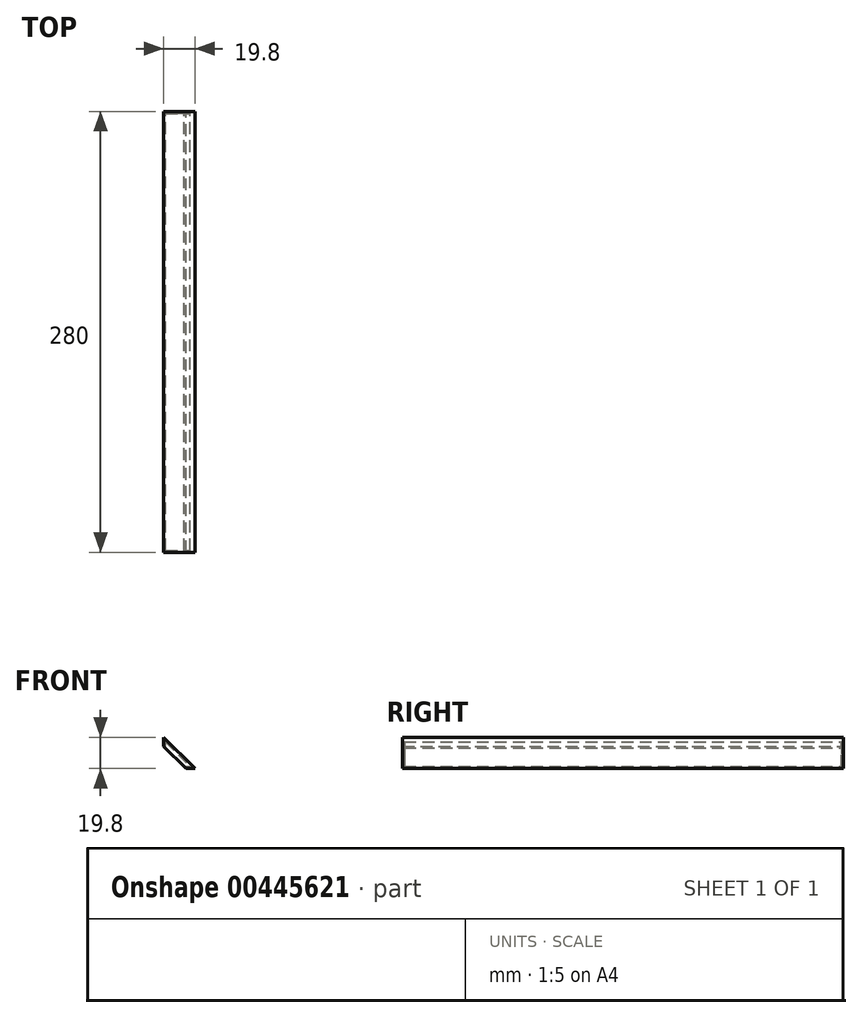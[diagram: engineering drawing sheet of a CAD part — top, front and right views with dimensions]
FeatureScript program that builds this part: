
annotation { "Feature Type Name" : "Feature", "Feature Type Description" : "" }
export const myFeature = defineFeature(function(context is Context, id is Id, definition is map)
    precondition{}
    {
        {
            var Q0;
            Q0=qCreatedBy(makeId("Front.planeOp"),FACE);
            var sketch = newSketch(context, id + "F0", { "sketchPlane" : qUnion([Q0])});
            skLineSegment(sketch, "E0.bottom", {"start": v(-9.9, -9.9) * mm, "end": v(9.9, -9.9) * mm});
            skLineSegment(sketch, "E0.top", {"start": v(-9.9, 9.9) * mm, "end": v(9.9, 9.9) * mm});
            skLineSegment(sketch, "E0.left", {"start": v(-9.9, -9.9) * mm, "end": v(-9.9, 9.9) * mm});
            skLineSegment(sketch, "E0.right", {"start": v(9.9, -9.9) * mm, "end": v(9.9, 9.9) * mm});
            skPoint(sketch, "E0.middle", {"position": v(0, 0) * mm});
            skLineSegment(sketch, "E1", {"start": v(-9.9, 9.9) * mm, "end": v(9.9, -9.9) * mm});
            skSolve(sketch);
        }
        {
            var Q0;
            Q0=makeQuery(id+"F0.imprint","IMPRINT",FACE,{"disambiguationData":[TD([[makeQuery(id+"F0.imprint","IMPRINT",EDGE,{"derivedFrom":sQuery(id+"F0.wireOp",EDGE,"E0.bottom")}),1.0]])]});
            extrude(context, id + "F1", {"entities" : qUnion([Q0]), "depth" : 280 * mm});
        }
        {
            var Q0;
            Q0=makeQuery(id+"F1.opExtrude","CAP_FACE",FACE,{"disambiguationData":[OSD([sQuery(id+"F0.wireOp",EDGE,"E0.bottom"),sQuery(id+"F0.wireOp",EDGE,"E0.left"),sQuery(id+"F0.wireOp",EDGE,"E1")])],"isStart":true});
            var sketch = newSketch(context, id + "F2", { "sketchPlane" : qUnion([Q0])});
            skLineSegment(sketch, "E2", {"start": v(-4.24, -9.9) * mm, "end": v(9.9, 4.24) * mm});
            skLineSegment(sketch, "E3.0.0", {"start": v(9.9, 9.9) * mm, "end": v(-9.9, -9.9) * mm});
            skLineSegment(sketch, "E3.0.1", {"start": v(-9.9, -9.9) * mm, "end": v(9.9, -9.9) * mm});
            skLineSegment(sketch, "E3.0.2", {"start": v(9.9, -9.9) * mm, "end": v(9.9, 9.9) * mm});
            skSolve(sketch);
        }
        {
            var Q0;
            {var subQ0=sQuery(id+"F2.wireOp",EDGE,"E2");Q0=makeQuery(id+"F2.imprint","IMPRINT",FACE,{"disambiguationData":[TD([[makeQuery(id+"F2.imprint","IMPRINT",EDGE,{"derivedFrom":subQ0}),-1.0]])]});}
            extrude(context, id + "F3", {"entities" : qUnion([Q0]), "operationType" : NewBodyOperationType.REMOVE, "oppositeDirection" : true, "depth" : 287 * mm});
        }
        {
            var Q0;
            Q0=makeQuery(id+"F3.boolean.opBoolean","COPY",FACE,{"derivedFrom":makeQuery(id+"F3.opExtrude","SWEPT_FACE",FACE,{"disambiguationData":[OSD([sQuery(id+"F2.wireOp",EDGE,"E2")])]})});
            shell(context, id + "F4", {"entities" : qUnion([Q0]), "thickness" : 1.2 * mm});
        }
    });
